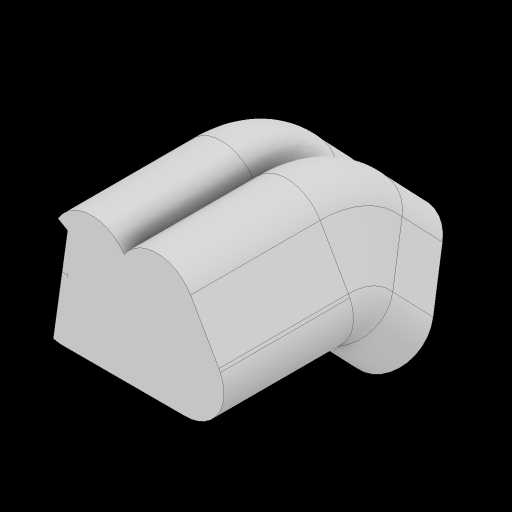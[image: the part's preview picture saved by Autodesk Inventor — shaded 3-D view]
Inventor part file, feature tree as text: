
AUTODESK INVENTOR PART (.ipt)
format: ipt  version: 2023 (Build 270158000, 158)  size: 465,920 bytes
history: native  units: mm
features: extrude x11, sketch x8, plane x3, chamfer x2, mirror x1, revolve x1
ambient origin geometry x8: Origin, YZ Plane, XZ Plane, XY Plane, X Axis, Y Axis, Z Axis, Center Point
bodies: Solid1 (feature_tree)
feature tree (26):
  sketch  "Sketch1"  dims[d0=100.0mm d1=25.0mm d2=7.5mm d3=7.5mm d4=60.0deg d5=15.0mm d6=11.0mm d7=11.0mm d8=15.0mm d14=4.0mm d15=0.0mm]
  extrude  "Extrusion1"  Depth=15.0mm TaperAngle=0.0deg
  plane  "Work Plane13"
  sketch  "Sketch7"  dims[d72=7.5mm d73=90.0deg]
  extrude  "Extrusion6"  TaperAngle=90.0deg  [1 undecoded]
  extrude  "Extrusion7"  Depth=7.5mm
  mirror  "Mirror4"
  plane  "Work Plane9"
  extrude  "Extrusion8"  Depth=15.0mm
  revolve  "Revolution2"  [1 undecoded]
  extrude  "Extrusion9"  Depth=6.5mm
  extrude  "Extrusion10"  Depth=10.0mm TaperAngle=0.0deg
  extrude  "Extrusion11"  Depth=15.0mm TaperAngle=0.0deg
  chamfer  "Chamfer3"  Distance=8.648979mm
  chamfer  "Chamfer4"  Distance=4.0mm
  plane  "Work Plane16"
  extrude  "Extrusion14"  Depth=10.0mm TaperAngle=0.0deg
  extrude  "Extrusion15"  Depth=10.0mm TaperAngle=0.0deg
  sketch  "Sketch25"  dims[d93=10.0mm d94=0.0mm d115=20.0mm d116=0.0mm d131=8.648979mm d132=4.0mm d133=0.0mm d134=10.0mm d135=0.0mm d136=10.0mm d137=0.0mm d138=2.0mm d139=4.0mm d140=45.0deg d141=2.0mm d142=4.0mm d143=45.0deg d153=15.0mm d154=15.0mm d155=15.0mm d156=25.0mm d157=0.0mm d158=20.0mm d160=20.0mm d161=10.0mm d165=240.642mm d168=30.0mm d169=0.0mm d173=2.0mm d174=1.413272mm d176=15.0mm d177=5.5mm d178=2.0mm d179=0.0mm d180=15.0mm d181=0.0mm d221=10.93871mm d222=47.979859mm d223=260.34779mm d182=0.5mm d183=0.872665mm d184=0.5mm d185=0.872665mm]
  extrude  "Extrusion17"  Depth=15.0mm TaperAngle=45.0deg
  extrude  "Extrusion18"  Depth=15.0mm TaperAngle=45.0deg
  sketch  "Sketch14"  dims[d74=7.5mm d75=5.5mm]
  sketch  "Sketch15"  dims[d76=5.5mm d77=15.0mm]
  sketch  "Sketch19"  dims[d78=11.0mm d79=11.0mm]
  sketch  "Sketch23"  dims[d80=2.0mm d81=6.5mm]
  sketch  "Sketch24"  dims[d82=6.5mm d83=10.0mm d84=0.0mm]
note: 2 required parameter values undecoded (feature->parameter linkage not recoverable at this tier; creation-order binding heuristic only, values carry confidence <= 0.55)